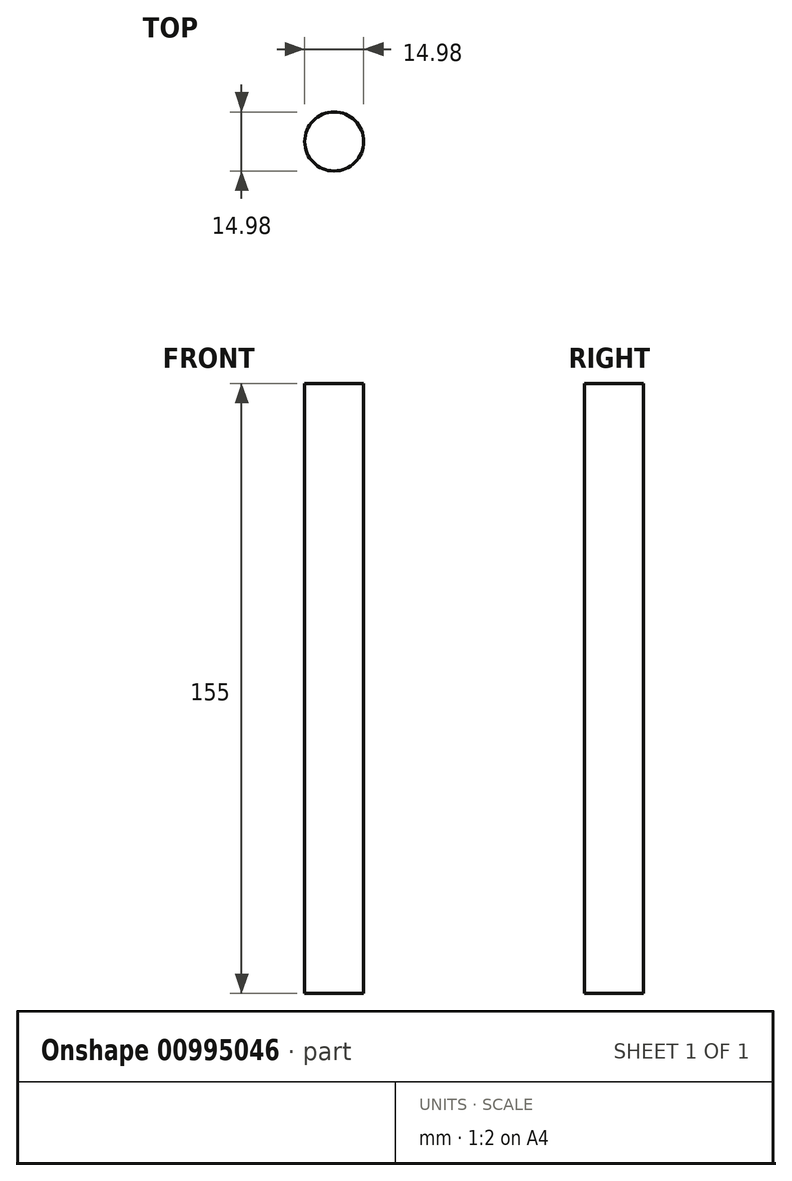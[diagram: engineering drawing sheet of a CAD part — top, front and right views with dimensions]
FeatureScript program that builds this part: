
annotation { "Feature Type Name" : "Feature", "Feature Type Description" : "" }
export const myFeature = defineFeature(function(context is Context, id is Id, definition is map)
    precondition{}
    {
        {
            var Q0;
            Q0=qCreatedBy(makeId("Top.planeOp"),FACE);
            var sketch = newSketch(context, id + "F0", { "sketchPlane" : qUnion([Q0])});
            skCircle(sketch, "E0", {"center": v(0, 0) * mm, "radius": 7.5 * mm});
            skSolve(sketch);
        }
        {
            var Q0;
            Q0=makeQuery(id+"F0.imprint","IMPRINT",FACE,{"disambiguationData":[TD([[makeQuery(id+"F0.imprint","IMPRINT",EDGE,{"derivedFrom":sQuery(id+"F0.wireOp",EDGE,"E0")}),1.0]])]});
            extrude(context, id + "F1", {"entities" : qUnion([Q0]), "depth" : 155 * mm, "offsetDistance" : 25 * mm});
        }
    });
